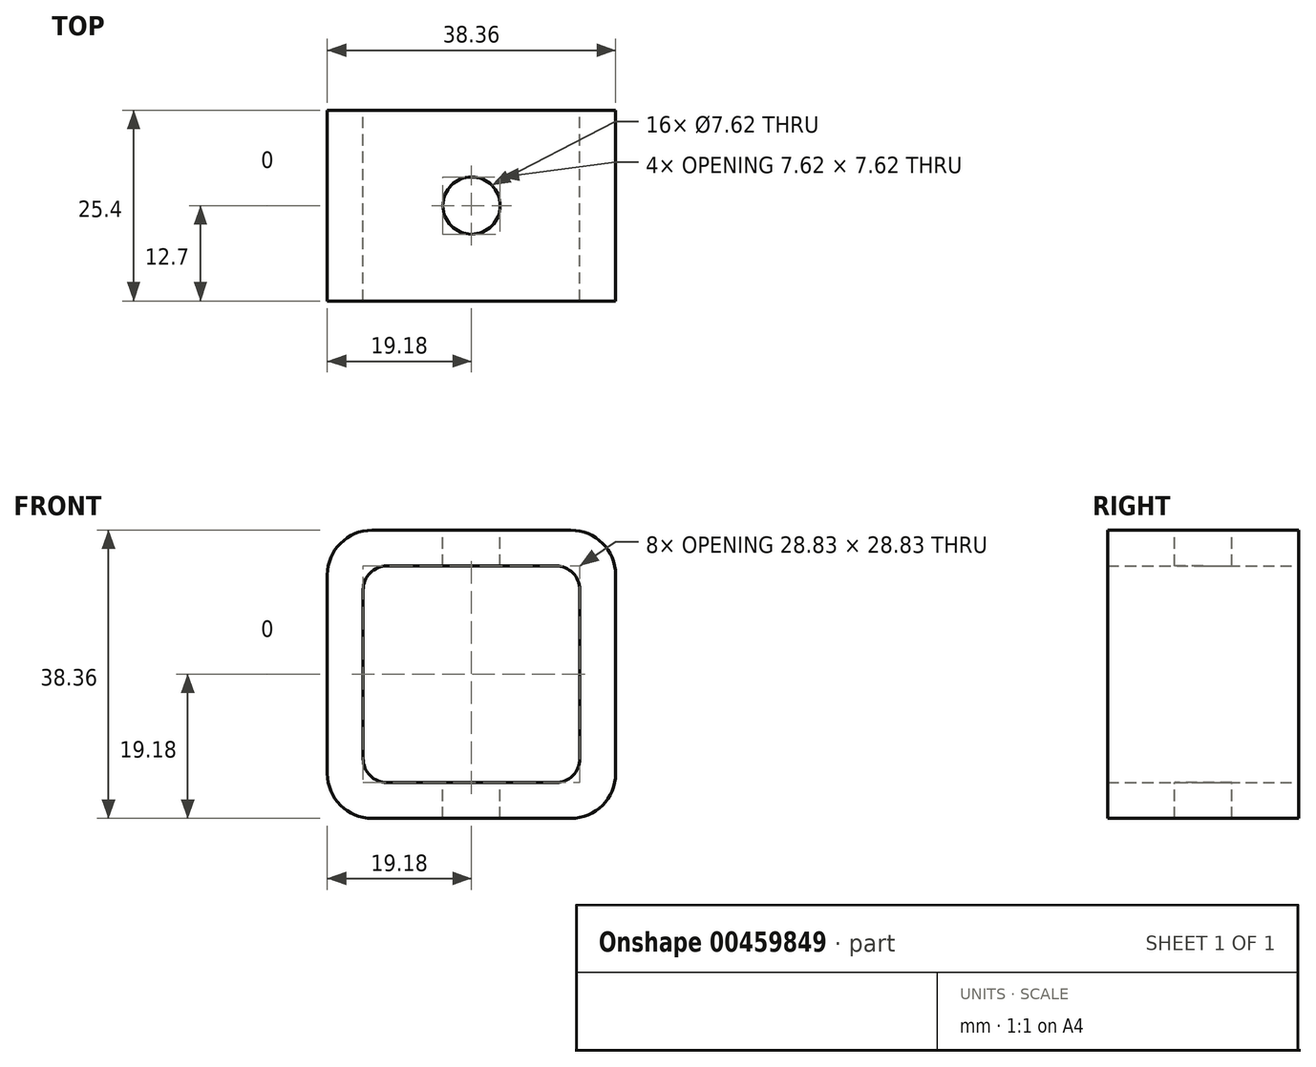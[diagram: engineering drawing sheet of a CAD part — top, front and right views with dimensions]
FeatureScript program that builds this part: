
annotation { "Feature Type Name" : "Feature", "Feature Type Description" : "" }
export const myFeature = defineFeature(function(context is Context, id is Id, definition is map)
    precondition{}
    {
        {
            var Q0;
            Q0=qCreatedBy(makeId("Front.planeOp"),FACE);
            var sketch = newSketch(context, id + "F0", { "sketchPlane" : qUnion([Q0])});
            skLineSegment(sketch, "E0.bottom", {"start": v(19.18, 19.18) * mm, "end": v(-19.18, 19.18) * mm});
            skLineSegment(sketch, "E0.top", {"start": v(19.18, -19.18) * mm, "end": v(-19.18, -19.18) * mm});
            skLineSegment(sketch, "E0.left", {"start": v(19.18, 19.18) * mm, "end": v(19.18, -19.18) * mm});
            skLineSegment(sketch, "E0.right", {"start": v(-19.18, 19.18) * mm, "end": v(-19.18, -19.18) * mm});
            skPoint(sketch, "E0.middle", {"position": v(0, 0) * mm});
            skLineSegment(sketch, "E1.0", {"start": v(-14.41, 14.41) * mm, "end": v(-14.41, -14.41) * mm});
            skLineSegment(sketch, "E1.1", {"start": v(14.41, 14.41) * mm, "end": v(-14.41, 14.41) * mm});
            skLineSegment(sketch, "E1.2", {"start": v(14.41, 14.41) * mm, "end": v(14.41, -14.41) * mm});
            skLineSegment(sketch, "E1.3", {"start": v(14.41, -14.41) * mm, "end": v(-14.41, -14.41) * mm});
            skSolve(sketch);
        }
        {
            var Q0;
            Q0=makeQuery(id+"F0.imprint","IMPRINT",FACE,{"disambiguationData":[TD([[makeQuery(id+"F0.imprint","IMPRINT",EDGE,{"derivedFrom":sQuery(id+"F0.wireOp",EDGE,"E0.bottom")}),1.0]])]});
            extrude(context, id + "F1", {"entities" : qUnion([Q0]), "endBound" : BoundingType.SYMMETRIC, "depth" : 25.4 * mm});
        }
        {
            var Q0;
            Q0=makeQuery(id+"F1.opExtrude","SWEPT_EDGE",EDGE,{"disambiguationData":[OSD([sQuery(id+"F0.wireOp",EDGE,"E0.bottom"),sQuery(id+"F0.wireOp",EDGE,"E0.right")])]});
            var Q1;
            Q1=makeQuery(id+"F1.opExtrude","SWEPT_EDGE",EDGE,{"disambiguationData":[OSD([sQuery(id+"F0.wireOp",EDGE,"E0.bottom"),sQuery(id+"F0.wireOp",EDGE,"E0.left")])]});
            var Q2;
            Q2=makeQuery(id+"F1.opExtrude","SWEPT_EDGE",EDGE,{"disambiguationData":[OSD([sQuery(id+"F0.wireOp",EDGE,"E0.top"),sQuery(id+"F0.wireOp",EDGE,"E0.left")])]});
            var Q3;
            Q3=makeQuery(id+"F1.opExtrude","SWEPT_EDGE",EDGE,{"disambiguationData":[OSD([sQuery(id+"F0.wireOp",EDGE,"E0.top"),sQuery(id+"F0.wireOp",EDGE,"E0.right")])]});
            fillet(context, id + "F2", {"entities" : qUnion([Q0, Q1, Q2, Q3]), "radius" : 5.97 * mm, "tangentPropagation" : true, "allowEdgeOverflow" : false});
        }
        {
            var Q0;
            Q0=makeQuery(id+"F1.opExtrude","SWEPT_EDGE",EDGE,{"disambiguationData":[OSD([sQuery(id+"F0.wireOp",EDGE,"E1.0"),sQuery(id+"F0.wireOp",EDGE,"E1.1")])]});
            var Q1;
            Q1=makeQuery(id+"F1.opExtrude","SWEPT_EDGE",EDGE,{"disambiguationData":[OSD([sQuery(id+"F0.wireOp",EDGE,"E1.1"),sQuery(id+"F0.wireOp",EDGE,"E1.2")])]});
            var Q2;
            Q2=makeQuery(id+"F1.opExtrude","SWEPT_EDGE",EDGE,{"disambiguationData":[OSD([sQuery(id+"F0.wireOp",EDGE,"E1.2"),sQuery(id+"F0.wireOp",EDGE,"E1.3")])]});
            var Q3;
            Q3=makeQuery(id+"F1.opExtrude","SWEPT_EDGE",EDGE,{"disambiguationData":[OSD([sQuery(id+"F0.wireOp",EDGE,"E1.0"),sQuery(id+"F0.wireOp",EDGE,"E1.3")])]});
            fillet(context, id + "F3", {"entities" : qUnion([Q0, Q1, Q2, Q3]), "radius" : 3.17 * mm, "tangentPropagation" : true, "allowEdgeOverflow" : false});
        }
        {
            var Q0;
            Q0=makeQuery(id+"F1.opExtrude","SWEPT_FACE",FACE,{"disambiguationData":[OSD([sQuery(id+"F0.wireOp",EDGE,"E0.bottom")])]});
            var sketch = newSketch(context, id + "F4", { "sketchPlane" : qUnion([Q0])});
            skCircle(sketch, "E2", {"center": v(0, 0) * mm, "radius": 3.81 * mm});
            skPoint(sketch, "E2.centerSnap0", {"position": v(13.2, 0) * mm});
            skPoint(sketch, "E2.centerSnap1", {"position": v(0, 12.7) * mm});
            skSolve(sketch);
        }
        {
            var Q0;
            Q0=qSketchRegion(id+"F4",true);
            extrude(context, id + "F5", {"entities" : qUnion([Q0]), "operationType" : NewBodyOperationType.REMOVE, "oppositeDirection" : true, "depth" : 43.69 * mm});
        }
    });
